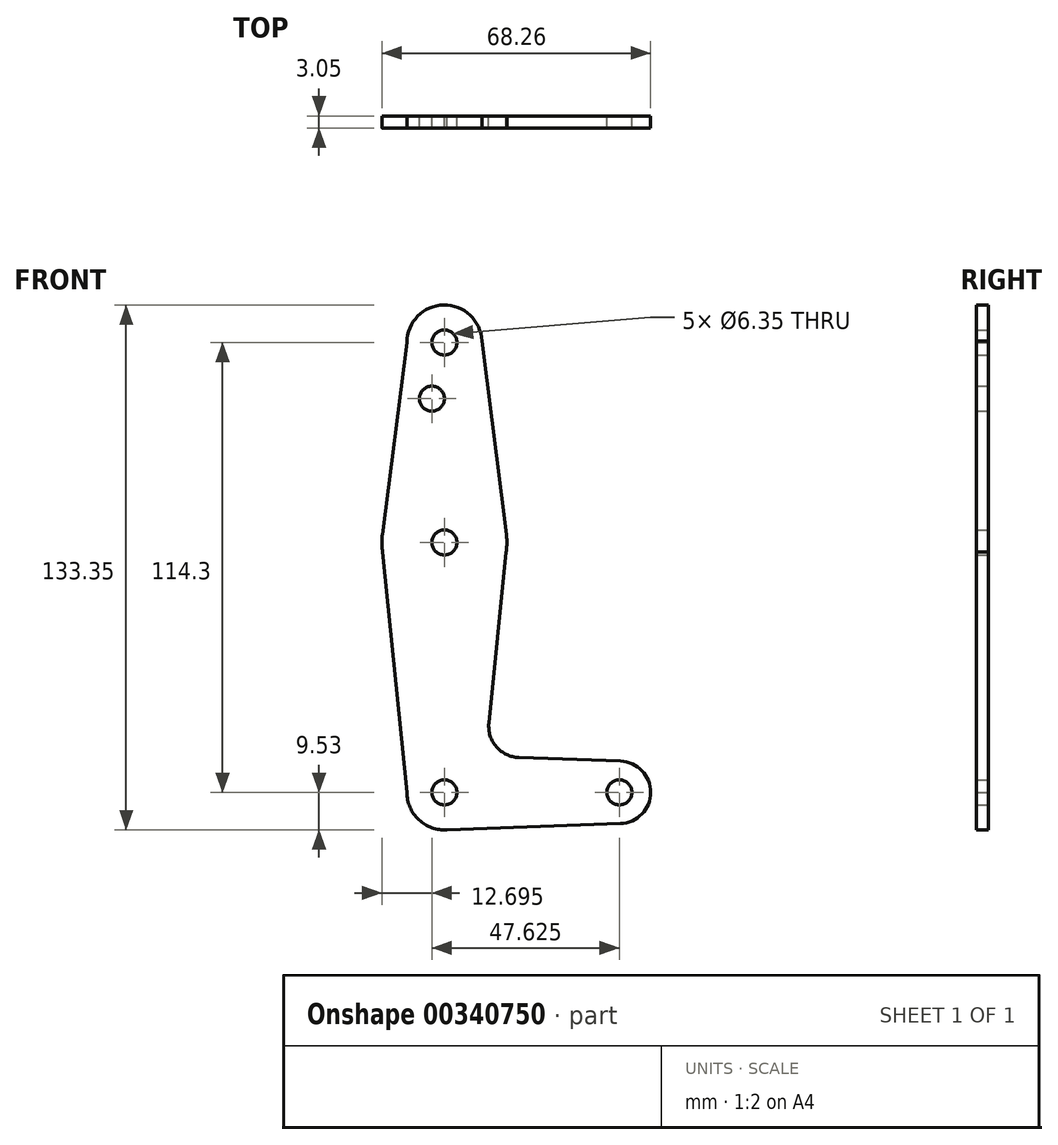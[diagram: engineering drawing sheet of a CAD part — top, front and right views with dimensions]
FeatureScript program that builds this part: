
annotation { "Feature Type Name" : "Feature", "Feature Type Description" : "" }
export const myFeature = defineFeature(function(context is Context, id is Id, definition is map)
    precondition{}
    {
        {
            var Q0;
            Q0=qCreatedBy(makeId("Front.planeOp"),FACE);
            var sketch = newSketch(context, id + "F0", { "sketchPlane" : qUnion([Q0])});
            skLineSegment(sketch, "E0", {"start": v(0, 50.8) * mm, "end": v(0, -63.5) * mm});
            skLineSegment(sketch, "E1", {"start": v(0, -63.5) * mm, "end": v(44.45, -63.5) * mm});
            skCircle(sketch, "E2", {"center": v(0, 50.8) * mm, "radius": 9.53 * mm});
            skCircle(sketch, "E3", {"center": v(0, 0) * mm, "radius": 15.88 * mm});
            skCircle(sketch, "E4", {"center": v(0, -63.5) * mm, "radius": 9.53 * mm});
            skCircle(sketch, "E5", {"center": v(44.45, -63.5) * mm, "radius": 7.94 * mm});
            skLineSegment(sketch, "E6", {"start": v(-9.52, 50.85) * mm, "end": v(-15.75, 2) * mm});
            skLineSegment(sketch, "E7", {"start": v(9.52, 51.23) * mm, "end": v(15.75, 2) * mm});
            skLineSegment(sketch, "E8", {"start": v(-9.53, -63.5) * mm, "end": v(-15.68, -2.46) * mm});
            skLineSegment(sketch, "E9", {"start": v(11.3, -45.9) * mm, "end": v(15.68, -2.46) * mm});
            skLineSegment(sketch, "E10", {"start": v(18.93, -54.65) * mm, "end": v(44.73, -55.57) * mm});
            skLineSegment(sketch, "E11", {"start": v(0, -73.02) * mm, "end": v(44.73, -71.43) * mm});
            skCircle(sketch, "E12", {"center": v(0, 50.8) * mm, "radius": 3.18 * mm});
            skCircle(sketch, "E13", {"center": v(0, 0) * mm, "radius": 3.18 * mm});
            skCircle(sketch, "E14", {"center": v(0, -63.5) * mm, "radius": 3.18 * mm});
            skCircle(sketch, "E15", {"center": v(44.45, -63.5) * mm, "radius": 3.18 * mm});
            skCircle(sketch, "E16", {"center": v(-3.18, 36.53) * mm, "radius": 3.18 * mm});
            skArc(sketch, "E17.filletArc", {"start": v(11.3, -45.9) * mm, "mid": v(13.22, -51.93) * mm, "end": v(18.93, -54.65) * mm});
            skSolve(sketch);
        }
        {
            var Q0;
            Q0 = qSketchRegion(id + "F0", true);
            var Q1;
            {var subQ0=sQuery(id+"F0.wireOp",EDGE,"E4");var subQ1=sQuery(id+"F0.wireOp",EDGE,"E0");var subQ2=makeQuery(id+"F0.imprint","INTERSECT",VERTEX,{"derivedFrom":[subQ1,subQ0]});Q1=makeQuery(id+"F0.imprint","IMPRINT",FACE,{"disambiguationData":[TD([[makeQuery(id+"F0.imprint","IMPRINT",EDGE,{"disambiguationData":[TD([[subQ2,-1.0]])],"derivedFrom":subQ1}),1.0]])]});}
            extrude(context, id + "F1", {"entities" : qUnion([Q0, Q1]), "depth" : 3.05 * mm});
        }
    });
